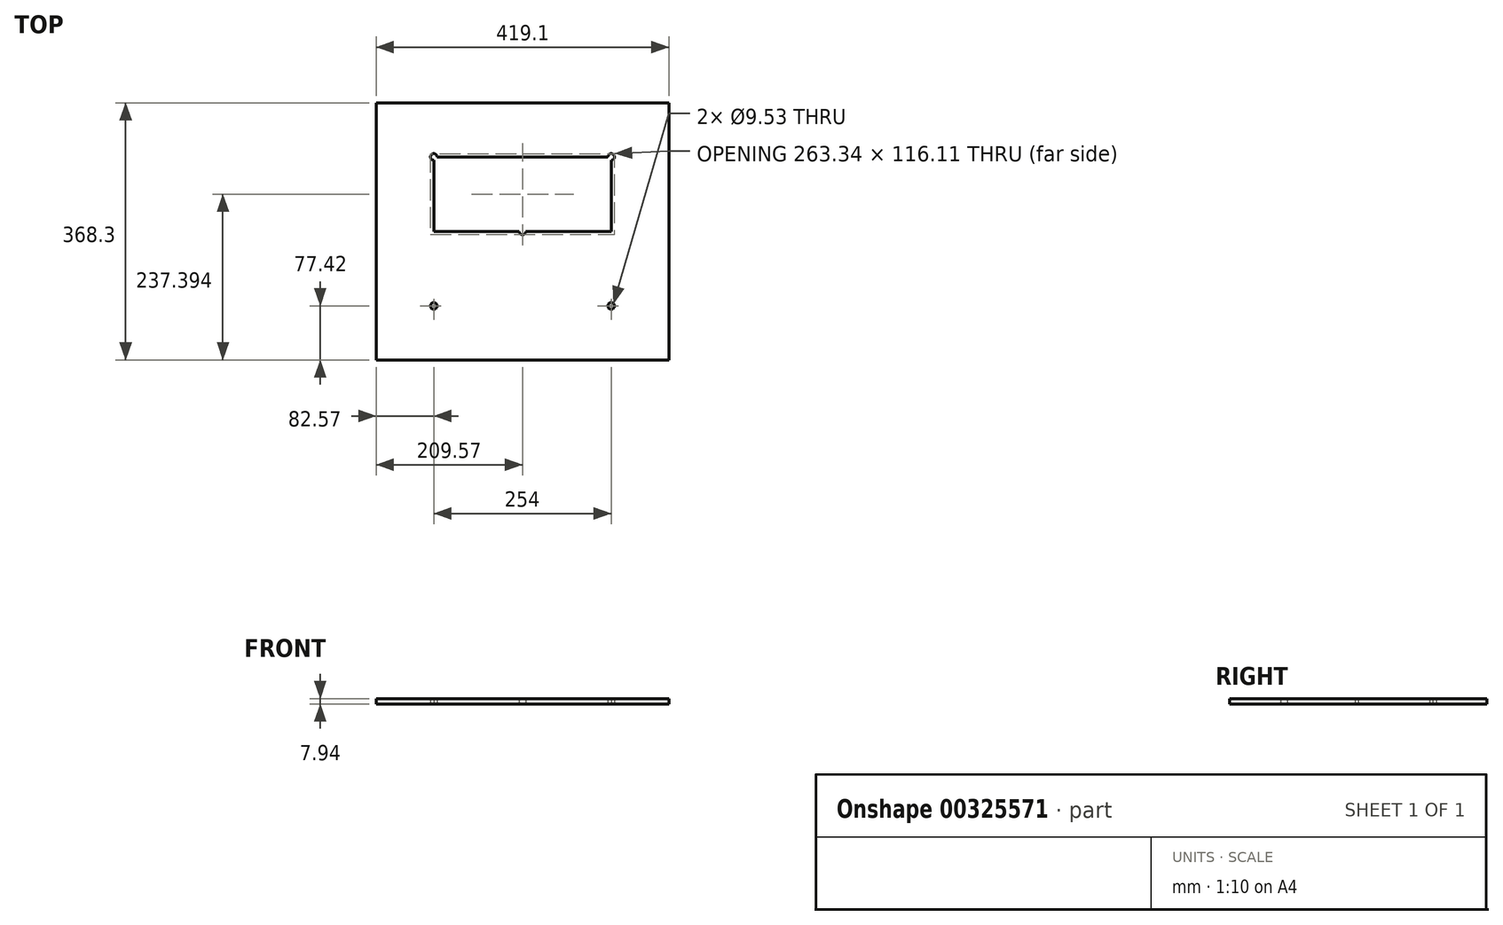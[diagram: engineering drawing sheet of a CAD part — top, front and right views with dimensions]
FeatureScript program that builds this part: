
annotation { "Feature Type Name" : "Feature", "Feature Type Description" : "" }
export const myFeature = defineFeature(function(context is Context, id is Id, definition is map)
    precondition{}
    {
        {
            var Q0;
            Q0=qCreatedBy(makeId("Top.planeOp"),FACE);
            var sketch = newSketch(context, id + "F0", { "sketchPlane" : qUnion([Q0])});
            skLineSegment(sketch, "E0.bottom", {"start": v(-209.57, 184.2) * mm, "end": v(209.53, 184.2) * mm});
            skLineSegment(sketch, "E0.top", {"start": v(-209.57, -184.1) * mm, "end": v(209.53, -184.1) * mm});
            skLineSegment(sketch, "E0.left", {"start": v(-209.57, 184.2) * mm, "end": v(-209.57, -184.1) * mm});
            skLineSegment(sketch, "E0.right", {"start": v(209.53, 184.2) * mm, "end": v(209.53, -184.1) * mm});
            skPoint(sketch, "E1", {"position": v(-0.02, -184.1) * mm});
            skPoint(sketch, "E2", {"position": v(209.53, 0.05) * mm});
            skPoint(sketch, "E3.start.orphan", {"position": v(-268.88, 0) * mm});
            skPoint(sketch, "E4.start.orphan", {"position": v(0, -219.65) * mm});
            skCircle(sketch, "E5", {"center": v(0, 0) * mm, "radius": 4.76 * mm});
            skLineSegment(sketch, "E6", {"start": v(-127, 259.43) * mm, "end": v(-127, -231.27) * mm});
            skLineSegment(sketch, "E7", {"start": v(0, 267.18) * mm, "end": v(0, -251.57) * mm});
            skLineSegment(sketch, "E8", {"start": v(127, 261.27) * mm, "end": v(127, -243.45) * mm});
            skLineSegment(sketch, "E9", {"start": v(-268.88, 0) * mm, "end": v(282.24, 0) * mm});
            skLineSegment(sketch, "E10", {"start": v(-273.4, 106.68) * mm, "end": v(267.11, 106.68) * mm});
            skLineSegment(sketch, "E11", {"start": v(-266.98, -106.68) * mm, "end": v(260.7, -106.68) * mm});
            skCircle(sketch, "E12", {"center": v(-127, 106.68) * mm, "radius": 4.76 * mm});
            skCircle(sketch, "E13", {"center": v(127, 106.68) * mm, "radius": 4.76 * mm});
            skCircle(sketch, "E14", {"center": v(127, -106.68) * mm, "radius": 4.76 * mm});
            skCircle(sketch, "E15", {"center": v(-127, -106.68) * mm, "radius": 4.76 * mm});
            skSolve(sketch);
        }
        {
            var Q0;
            {var subQ1=sQuery(id+"F0.wireOp",EDGE,"E0.top");var subQ6=sQuery(id+"F0.wireOp",EDGE,"E0.left");var subQ9=makeQuery(id+"F0.imprint","INTERSECT",VERTEX,{"derivedFrom":[subQ1,subQ6]});Q0=makeQuery(id+"F0.imprint","IMPRINT",FACE,{"disambiguationData":[TD([[makeQuery(id+"F0.imprint","IMPRINT",EDGE,{"disambiguationData":[TD([[subQ9,-1.0]])],"derivedFrom":subQ1}),1.0]])]});}
            var Q1;
            {var subQ5=sQuery(id+"F0.wireOp",EDGE,"E0.top");var subQ7=sQuery(id+"F0.wireOp",EDGE,"E6");var subQ8=makeQuery(id+"F0.imprint","INTERSECT",VERTEX,{"derivedFrom":[subQ5,subQ7]});Q1=makeQuery(id+"F0.imprint","IMPRINT",FACE,{"disambiguationData":[TD([[makeQuery(id+"F0.imprint","IMPRINT",EDGE,{"disambiguationData":[TD([[subQ8,-1.0]])],"derivedFrom":subQ5}),1.0]])]});}
            var Q2;
            {var subQ1=sQuery(id+"F0.wireOp",EDGE,"E5");var subQ5=sQuery(id+"F0.wireOp",EDGE,"E9");var subQ6=makeQuery(id+"F0.imprint","INTERSECT",VERTEX,{"disambiguationData":[OD(1.0)],"derivedFrom":[subQ1,subQ5]});Q2=makeQuery(id+"F0.imprint","IMPRINT",FACE,{"disambiguationData":[TD([[makeQuery(id+"F0.imprint","IMPRINT",EDGE,{"disambiguationData":[TD([[subQ6,-1.0]])],"derivedFrom":subQ1}),-1.0]])]});}
            var Q3;
            {var subQ1=sQuery(id+"F0.wireOp",EDGE,"E0.left");var subQ5=sQuery(id+"F0.wireOp",EDGE,"E9");var subQ6=makeQuery(id+"F0.imprint","INTERSECT",VERTEX,{"derivedFrom":[subQ1,subQ5]});Q3=makeQuery(id+"F0.imprint","IMPRINT",FACE,{"disambiguationData":[TD([[makeQuery(id+"F0.imprint","IMPRINT",EDGE,{"disambiguationData":[TD([[subQ6,-1.0]])],"derivedFrom":subQ1}),1.0]])]});}
            var Q4;
            {var subQ1=sQuery(id+"F0.wireOp",EDGE,"E0.left");var subQ5=sQuery(id+"F0.wireOp",EDGE,"E10");var subQ6=makeQuery(id+"F0.imprint","INTERSECT",VERTEX,{"derivedFrom":[subQ1,subQ5]});Q4=makeQuery(id+"F0.imprint","IMPRINT",FACE,{"disambiguationData":[TD([[makeQuery(id+"F0.imprint","IMPRINT",EDGE,{"disambiguationData":[TD([[subQ6,-1.0]])],"derivedFrom":subQ1}),1.0]])]});}
            var Q5;
            {var subQ0=sQuery(id+"F0.wireOp",EDGE,"E7");var subQ1=sQuery(id+"F0.wireOp",EDGE,"E5");var subQ2=makeQuery(id+"F0.imprint","INTERSECT",VERTEX,{"disambiguationData":[OD(0.0)],"derivedFrom":[subQ1,subQ0]});Q5=makeQuery(id+"F0.imprint","IMPRINT",FACE,{"disambiguationData":[TD([[makeQuery(id+"F0.imprint","IMPRINT",EDGE,{"disambiguationData":[TD([[subQ2,-1.0]])],"derivedFrom":subQ1}),-1.0]])]});}
            var Q6;
            {var subQ1=sQuery(id+"F0.wireOp",EDGE,"E0.bottom");var subQ5=sQuery(id+"F0.wireOp",EDGE,"E6");var subQ6=makeQuery(id+"F0.imprint","INTERSECT",VERTEX,{"derivedFrom":[subQ1,subQ5]});Q6=makeQuery(id+"F0.imprint","IMPRINT",FACE,{"disambiguationData":[TD([[makeQuery(id+"F0.imprint","IMPRINT",EDGE,{"disambiguationData":[TD([[subQ6,-1.0]])],"derivedFrom":subQ1}),-1.0]])]});}
            var Q7;
            {var subQ1=sQuery(id+"F0.wireOp",EDGE,"E0.left");var subQ5=sQuery(id+"F0.wireOp",EDGE,"E0.bottom");var subQ6=makeQuery(id+"F0.imprint","INTERSECT",VERTEX,{"derivedFrom":[subQ5,subQ1]});Q7=makeQuery(id+"F0.imprint","IMPRINT",FACE,{"disambiguationData":[TD([[makeQuery(id+"F0.imprint","IMPRINT",EDGE,{"disambiguationData":[TD([[subQ6,-1.0]])],"derivedFrom":subQ5}),-1.0]])]});}
            var Q8;
            {var subQ1=sQuery(id+"F0.wireOp",EDGE,"E0.right");var subQ6=sQuery(id+"F0.wireOp",EDGE,"E0.bottom");var subQ9=makeQuery(id+"F0.imprint","INTERSECT",VERTEX,{"derivedFrom":[subQ6,subQ1]});Q8=makeQuery(id+"F0.imprint","IMPRINT",FACE,{"disambiguationData":[TD([[makeQuery(id+"F0.imprint","IMPRINT",EDGE,{"disambiguationData":[TD([[subQ9,1.0]])],"derivedFrom":subQ6}),-1.0]])]});}
            var Q9;
            {var subQ1=sQuery(id+"F0.wireOp",EDGE,"E0.bottom");var subQ5=sQuery(id+"F0.wireOp",EDGE,"E7");var subQ6=makeQuery(id+"F0.imprint","INTERSECT",VERTEX,{"derivedFrom":[subQ1,subQ5]});Q9=makeQuery(id+"F0.imprint","IMPRINT",FACE,{"disambiguationData":[TD([[makeQuery(id+"F0.imprint","IMPRINT",EDGE,{"disambiguationData":[TD([[subQ6,-1.0]])],"derivedFrom":subQ1}),-1.0]])]});}
            var Q10;
            {var subQ7=sQuery(id+"F0.wireOp",EDGE,"E7");var subQ8=sQuery(id+"F0.wireOp",EDGE,"E5");var subQ9=makeQuery(id+"F0.imprint","INTERSECT",VERTEX,{"disambiguationData":[OD(0.0)],"derivedFrom":[subQ8,subQ7]});Q10=makeQuery(id+"F0.imprint","IMPRINT",FACE,{"disambiguationData":[TD([[makeQuery(id+"F0.imprint","IMPRINT",EDGE,{"disambiguationData":[TD([[subQ9,1.0]])],"derivedFrom":subQ8}),-1.0]])]});}
            var Q11;
            {var subQ0=sQuery(id+"F0.wireOp",EDGE,"E10");var subQ1=sQuery(id+"F0.wireOp",EDGE,"E0.right");var subQ2=makeQuery(id+"F0.imprint","INTERSECT",VERTEX,{"derivedFrom":[subQ1,subQ0]});Q11=makeQuery(id+"F0.imprint","IMPRINT",FACE,{"disambiguationData":[TD([[makeQuery(id+"F0.imprint","IMPRINT",EDGE,{"disambiguationData":[TD([[subQ2,-1.0]])],"derivedFrom":subQ1}),-1.0]])]});}
            var Q12;
            {var subQ0=sQuery(id+"F0.wireOp",EDGE,"E9");var subQ1=sQuery(id+"F0.wireOp",EDGE,"E5");var subQ2=makeQuery(id+"F0.imprint","INTERSECT",VERTEX,{"disambiguationData":[OD(0.0)],"derivedFrom":[subQ1,subQ0]});Q12=makeQuery(id+"F0.imprint","IMPRINT",FACE,{"disambiguationData":[TD([[makeQuery(id+"F0.imprint","IMPRINT",EDGE,{"disambiguationData":[TD([[subQ2,1.0]])],"derivedFrom":subQ1}),-1.0]])]});}
            var Q13;
            {var subQ0=sQuery(id+"F0.wireOp",EDGE,"E9");var subQ1=sQuery(id+"F0.wireOp",EDGE,"E0.right");var subQ2=makeQuery(id+"F0.imprint","INTERSECT",VERTEX,{"derivedFrom":[subQ1,subQ0]});Q13=makeQuery(id+"F0.imprint","IMPRINT",FACE,{"disambiguationData":[TD([[makeQuery(id+"F0.imprint","IMPRINT",EDGE,{"disambiguationData":[TD([[subQ2,-1.0]])],"derivedFrom":subQ1}),-1.0]])]});}
            var Q14;
            {var subQ1=sQuery(id+"F0.wireOp",EDGE,"E7");var subQ5=sQuery(id+"F0.wireOp",EDGE,"E0.top");var subQ6=makeQuery(id+"F0.imprint","INTERSECT",VERTEX,{"derivedFrom":[subQ5,subQ1]});Q14=makeQuery(id+"F0.imprint","IMPRINT",FACE,{"disambiguationData":[TD([[makeQuery(id+"F0.imprint","IMPRINT",EDGE,{"disambiguationData":[TD([[subQ6,-1.0]])],"derivedFrom":subQ5}),1.0]])]});}
            var Q15;
            {var subQ1=sQuery(id+"F0.wireOp",EDGE,"E0.right");var subQ6=sQuery(id+"F0.wireOp",EDGE,"E0.top");var subQ9=makeQuery(id+"F0.imprint","INTERSECT",VERTEX,{"derivedFrom":[subQ6,subQ1]});Q15=makeQuery(id+"F0.imprint","IMPRINT",FACE,{"disambiguationData":[TD([[makeQuery(id+"F0.imprint","IMPRINT",EDGE,{"disambiguationData":[TD([[subQ9,1.0]])],"derivedFrom":subQ6}),1.0]])]});}
            extrude(context, id + "F1", {"entities" : qUnion([Q0, Q1, Q2, Q3, Q4, Q5, Q6, Q7, Q8, Q9, Q10, Q11, Q12, Q13, Q14, Q15]), "depth" : 7.94 * mm});
        }
    });
